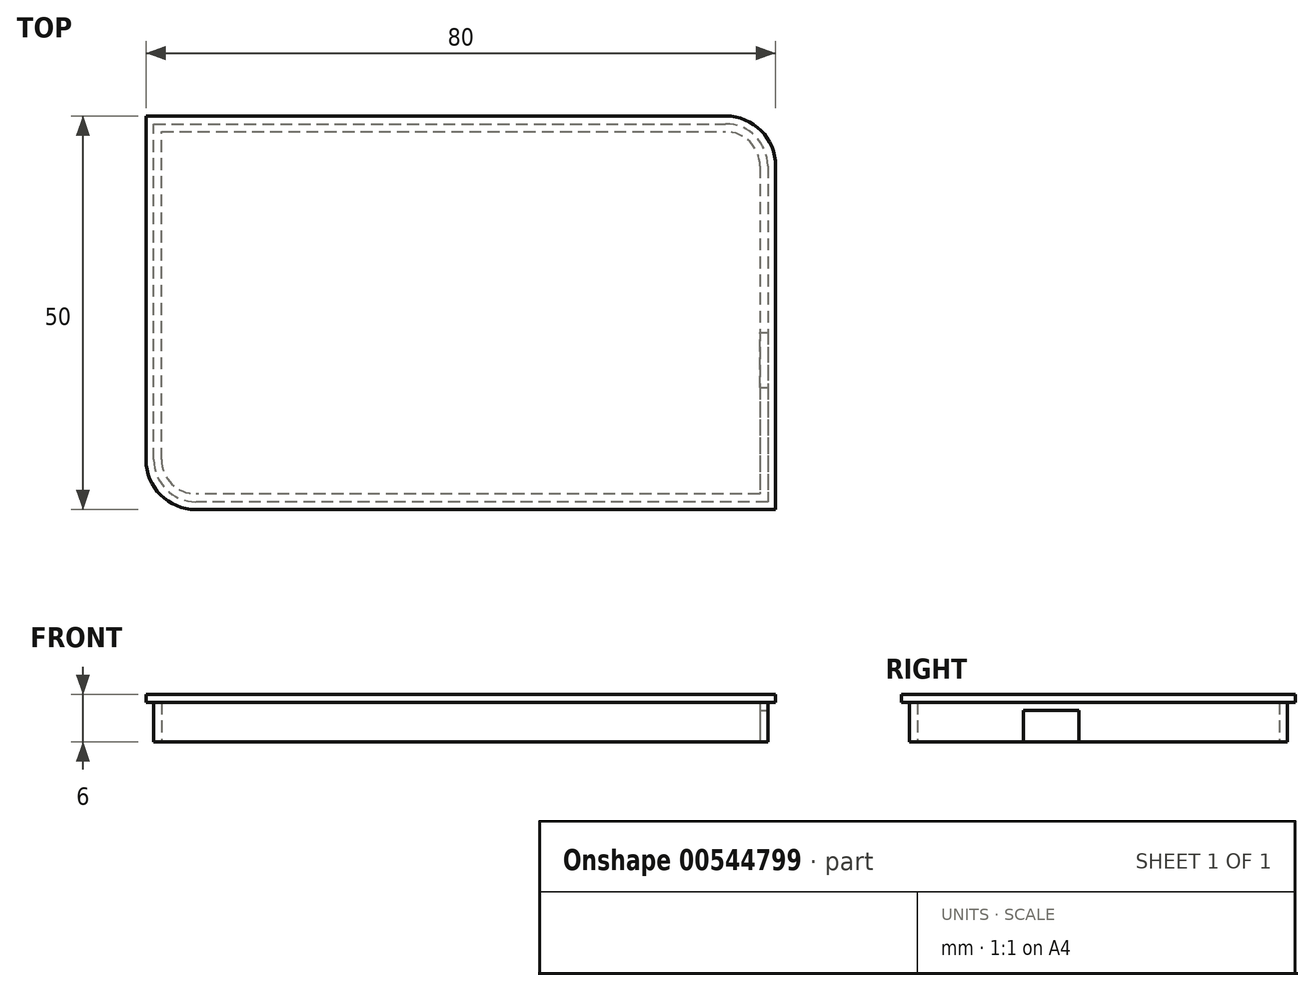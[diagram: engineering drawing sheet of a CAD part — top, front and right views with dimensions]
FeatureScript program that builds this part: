
annotation { "Feature Type Name" : "Feature", "Feature Type Description" : "" }
export const myFeature = defineFeature(function(context is Context, id is Id, definition is map)
    precondition{}
    {
        {
            var Q0;
            Q0=qCreatedBy(makeId("Top.planeOp"),FACE);
            var sketch = newSketch(context, id + "F0", { "sketchPlane" : qUnion([Q0])});
            skLineSegment(sketch, "E0.bottom", {"start": v(40, -25) * mm, "end": v(-33.65, -25) * mm});
            skLineSegment(sketch, "E0.top", {"start": v(33.65, 25) * mm, "end": v(-40, 25) * mm});
            skLineSegment(sketch, "E0.left", {"start": v(40, -25) * mm, "end": v(40, 18.65) * mm});
            skLineSegment(sketch, "E0.right", {"start": v(-40, -18.65) * mm, "end": v(-40, 25) * mm});
            skPoint(sketch, "E0.middle", {"position": v(0, 0) * mm});
            skPoint(sketch, "E1.visualSharp", {"position": v(-40, 25) * mm});
            skLineSegment(sketch, "E1.filletArc", {"start": v(-40, 25) * mm, "end": v(-40, 25) * mm});
            skPoint(sketch, "E2.visualSharp", {"position": v(40, -25) * mm});
            skLineSegment(sketch, "E2.filletArc", {"start": v(40, -25) * mm, "end": v(40, -25) * mm});
            skPoint(sketch, "E3.visualSharp", {"position": v(-40, -25) * mm});
            skArc(sketch, "E3.filletArc", {"start": v(-40, -18.65) * mm, "mid": v(-38.14, -23.14) * mm, "end": v(-33.65, -25) * mm});
            skPoint(sketch, "E4.visualSharp", {"position": v(40, 25) * mm});
            skArc(sketch, "E4.filletArc", {"start": v(40, 18.65) * mm, "mid": v(38.14, 23.14) * mm, "end": v(33.65, 25) * mm});
            skSolve(sketch);
        }
        {
            var Q0;
            Q0 = qSketchRegion(id + "F0", true);
            extrude(context, id + "F1", {"entities" : qUnion([Q0]), "depth" : 1 * mm, "offsetDistance" : 25.4 * mm});
        }
        {
            var Q0;
            Q0=makeQuery(id+"F1.opExtrude","CAP_FACE",FACE,{"disambiguationData":[OSD([sQuery(id+"F0.wireOp",EDGE,"E0.bottom"),sQuery(id+"F0.wireOp",EDGE,"E0.top"),sQuery(id+"F0.wireOp",EDGE,"E0.left"),sQuery(id+"F0.wireOp",EDGE,"E0.right"),sQuery(id+"F0.wireOp",EDGE,"E3.filletArc"),sQuery(id+"F0.wireOp",EDGE,"E4.filletArc")])],"isStart":true});
            var sketch = newSketch(context, id + "F2", { "sketchPlane" : qUnion([Q0])});
            skArc(sketch, "E5.0", {"start": v(-33.65, 24) * mm, "mid": v(-37.43, 22.43) * mm, "end": v(-39, 18.65) * mm});
            skLineSegment(sketch, "E5.1", {"start": v(-39, -24) * mm, "end": v(33.65, -24) * mm});
            skArc(sketch, "E5.2", {"start": v(33.65, -24) * mm, "mid": v(37.43, -22.43) * mm, "end": v(39, -18.65) * mm});
            skLineSegment(sketch, "E5.3", {"start": v(-39, 18.65) * mm, "end": v(-39, -24) * mm});
            skLineSegment(sketch, "E5.4", {"start": v(39, -18.65) * mm, "end": v(39, 24) * mm});
            skLineSegment(sketch, "E5.5", {"start": v(39, 24) * mm, "end": v(-33.65, 24) * mm});
            skSolve(sketch);
        }
        {
            var Q0;
            Q0 = qSketchRegion(id + "F2", true);
            extrude(context, id + "F3", {"entities" : qUnion([Q0]), "operationType" : NewBodyOperationType.ADD, "depth" : 5 * mm, "offsetDistance" : 25.4 * mm});
        }
        {
            var Q0;
            Q0=makeQuery(id+"F3.opExtrude","CAP_FACE",FACE,{"disambiguationData":[OSD([sQuery(id+"F2.wireOp",EDGE,"E5.0"),sQuery(id+"F2.wireOp",EDGE,"E5.1"),sQuery(id+"F2.wireOp",EDGE,"E5.2"),sQuery(id+"F2.wireOp",EDGE,"E5.3"),sQuery(id+"F2.wireOp",EDGE,"E5.4"),sQuery(id+"F2.wireOp",EDGE,"E5.5")])],"isStart":false});
            var sketch = newSketch(context, id + "F4", { "sketchPlane" : qUnion([Q0])});
            skLineSegment(sketch, "E6.0", {"start": v(-38, -23) * mm, "end": v(33.65, -23) * mm});
            skLineSegment(sketch, "E6.1", {"start": v(38, -18.65) * mm, "end": v(38, 23) * mm});
            skLineSegment(sketch, "E6.2", {"start": v(38, 23) * mm, "end": v(-33.65, 23) * mm});
            skArc(sketch, "E6.3", {"start": v(33.65, -23) * mm, "mid": v(36.73, -21.73) * mm, "end": v(38, -18.65) * mm});
            skArc(sketch, "E6.4", {"start": v(-33.65, 23) * mm, "mid": v(-36.73, 21.73) * mm, "end": v(-38, 18.65) * mm});
            skLineSegment(sketch, "E6.5", {"start": v(-38, 18.65) * mm, "end": v(-38, -23) * mm});
            skSolve(sketch);
        }
        {
            var Q0;
            Q0 = qSketchRegion(id + "F4", true);
            extrude(context, id + "F5", {"entities" : qUnion([Q0]), "operationType" : NewBodyOperationType.REMOVE, "oppositeDirection" : true, "depth" : 5 * mm, "offsetDistance" : 25.4 * mm});
        }
        {
            var Q0;
            Q0=makeQuery(id+"F3.opExtrude","SWEPT_FACE",FACE,{"disambiguationData":[OSD([sQuery(id+"F2.wireOp",EDGE,"E5.4")])]});
            var sketch = newSketch(context, id + "F6", { "sketchPlane" : qUnion([Q0])});
            skLineSegment(sketch, "E7.bottom", {"start": v(-2.5, -5) * mm, "end": v(-9.5, -5) * mm});
            skLineSegment(sketch, "E7.top", {"start": v(-2.5, -1) * mm, "end": v(-9.5, -1) * mm});
            skLineSegment(sketch, "E7.left", {"start": v(-2.5, -5) * mm, "end": v(-2.5, -1) * mm});
            skLineSegment(sketch, "E7.right", {"start": v(-9.5, -5) * mm, "end": v(-9.5, -1) * mm});
            skPoint(sketch, "E7.middle", {"position": v(-6, -3) * mm});
            skSolve(sketch);
        }
        {
            var Q0;
            Q0 = qSketchRegion(id + "F6", true);
            extrude(context, id + "F7", {"entities" : qUnion([Q0]), "operationType" : NewBodyOperationType.REMOVE, "endBound" : BoundingType.UP_TO_NEXT, "oppositeDirection" : true, "depth" : 25.4 * mm, "offsetDistance" : 25.4 * mm});
        }
    });
